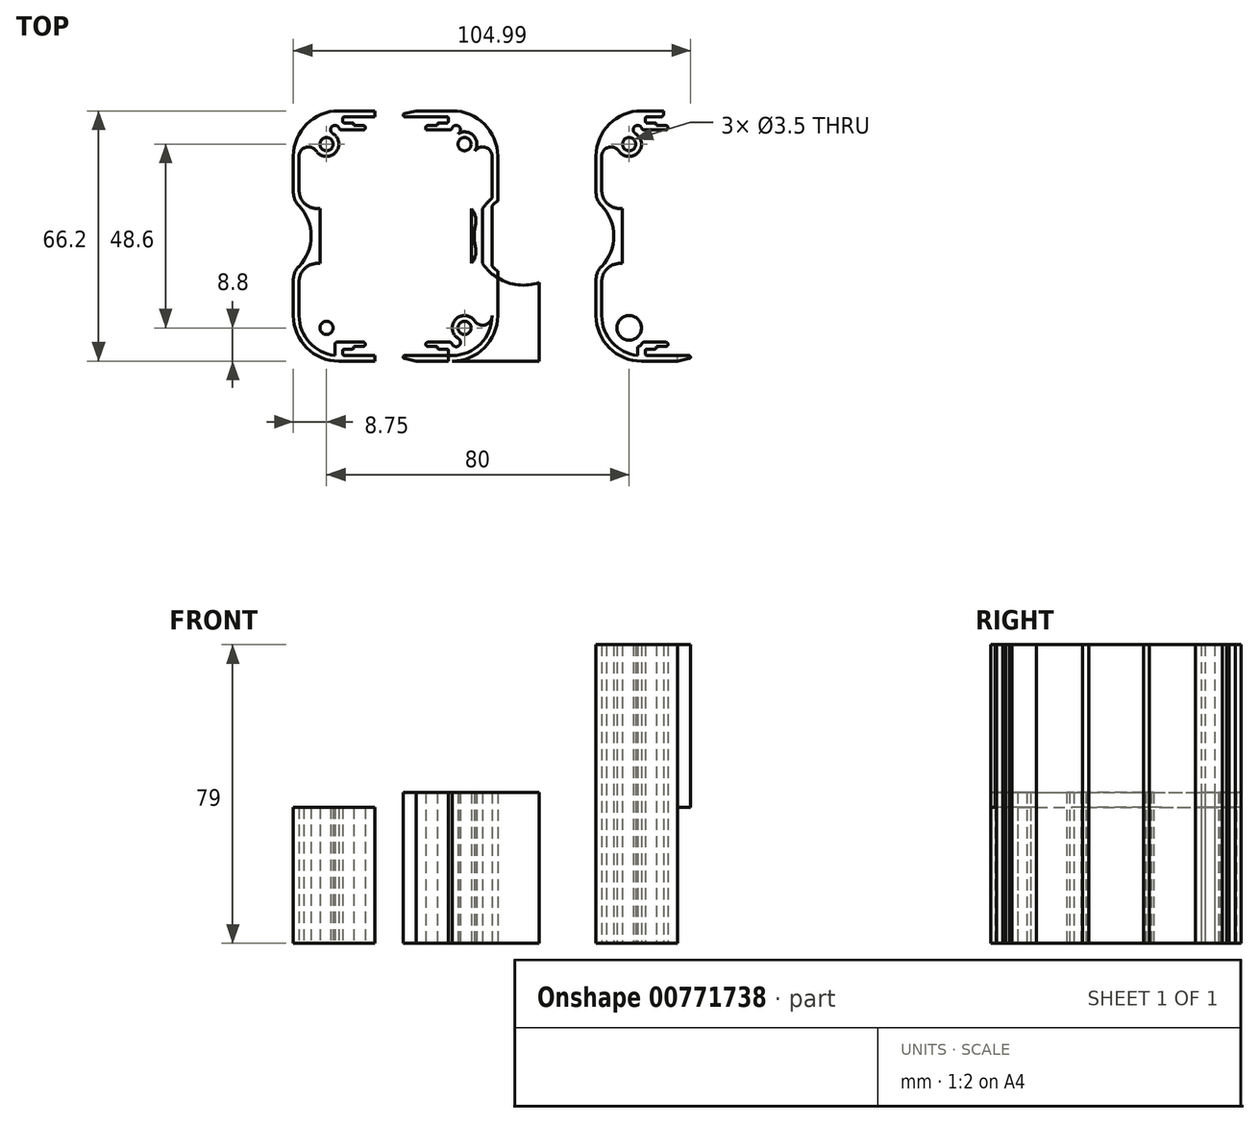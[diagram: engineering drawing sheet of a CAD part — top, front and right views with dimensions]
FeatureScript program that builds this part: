
annotation { "Feature Type Name" : "Feature", "Feature Type Description" : "" }
export const myFeature = defineFeature(function(context is Context, id is Id, definition is map)
    precondition{}
    {
        {
            var Q0;
            Q0=qCreatedBy(makeId("Top.planeOp"),FACE);
            var sketch = newSketch(context, id + "F0", { "sketchPlane" : qUnion([Q0])});
            skLineSegment(sketch, "E0.bottom", {"start": v(18, -33.1) * mm, "end": v(5, -33.1) * mm});
            skLineSegment(sketch, "E0.top", {"start": v(18, 33.1) * mm, "end": v(-18, 33.1) * mm});
            skLineSegment(sketch, "E0.left", {"start": v(18, -33.1) * mm, "end": v(18, 33.1) * mm});
            skLineSegment(sketch, "E0.right", {"start": v(-18, -33.1) * mm, "end": v(-18, 33.1) * mm});
            skPoint(sketch, "E0.middle", {"position": v(0, 0) * mm});
            skLineSegment(sketch, "E1.bottom", {"start": v(18, -33.1) * mm, "end": v(-18, -33.1) * mm});
            skLineSegment(sketch, "E1.right", {"start": v(-7, -21.1) * mm, "end": v(-7, 21.1) * mm});
            skPoint(sketch, "E2.visualSharp", {"position": v(-7, 33.1) * mm});
            skArc(sketch, "E2.filletArc", {"start": v(5, 33.1) * mm, "mid": v(-3.49, 29.59) * mm, "end": v(-7, 21.1) * mm});
            skPoint(sketch, "E3.newPointB", {"position": v(-18, -33.1) * mm});
            skArc(sketch, "E3.filletArc", {"start": v(-7, -21.1) * mm, "mid": v(-3.49, -29.59) * mm, "end": v(5, -33.1) * mm});
            skLineSegment(sketch, "E4.0", {"start": v(18, -31.6) * mm, "end": v(5, -31.6) * mm});
            skLineSegment(sketch, "E4.1", {"start": v(18, 31.55) * mm, "end": v(4, 31.55) * mm});
            skArc(sketch, "E4.2", {"start": v(4, 31.55) * mm, "mid": v(-2.77, 28.16) * mm, "end": v(-5.5, 21.1) * mm});
            skLineSegment(sketch, "E4.3", {"start": v(-5.5, -21.1) * mm, "end": v(-5.5, 21.1) * mm});
            skArc(sketch, "E4.4", {"start": v(-5.5, -21.1) * mm, "mid": v(-2.42, -28.52) * mm, "end": v(5, -31.6) * mm});
            skCircle(sketch, "E5", {"center": v(-13.8, 0) * mm, "radius": 11.5 * mm});
            skCircle(sketch, "E6.0", {"center": v(-13.8, 0) * mm, "radius": 13 * mm});
            skLineSegment(sketch, "E7", {"start": v(-2.3, 0) * mm, "end": v(-0.8, 0) * mm, "construction": true});
            skLineSegment(sketch, "E8.left", {"start": v(0, 7.25) * mm, "end": v(0, -7.25) * mm});
            skPoint(sketch, "E8.middle", {"position": v(-1.55, 0) * mm});
            skCircle(sketch, "E9", {"center": v(1.75, 24.3) * mm, "radius": 1.75 * mm});
            skCircle(sketch, "E10.0", {"center": v(1.75, 24.3) * mm, "radius": 3.25 * mm});
            skLineSegment(sketch, "E11.top", {"start": v(12, 28.1) * mm, "end": v(4, 28.1) * mm});
            skLineSegment(sketch, "E11.right", {"start": v(4, 33.1) * mm, "end": v(4, 28.1) * mm});
            skLineSegment(sketch, "E12.bottom", {"start": v(4, 28.1) * mm, "end": v(12, 28.1) * mm});
            skLineSegment(sketch, "E13.top", {"start": v(18, 31.55) * mm, "end": v(18, 31.55) * mm});
            skLineSegment(sketch, "E13.left", {"start": v(18, 31.55) * mm, "end": v(18, 31.55) * mm});
            skLineSegment(sketch, "E14.left", {"start": v(4, 28.1) * mm, "end": v(4, 31.55) * mm});
            skLineSegment(sketch, "E14.right", {"start": v(6, 29.9) * mm, "end": v(6, 33.1) * mm});
            skLineSegment(sketch, "E15.bottom", {"start": v(4, 28.1) * mm, "end": v(4, 28.1) * mm});
            skLineSegment(sketch, "E15.top", {"start": v(6, 29.9) * mm, "end": v(9, 29.9) * mm});
            skLineSegment(sketch, "E15.right", {"start": v(9, 29.2) * mm, "end": v(9, 29.9) * mm});
            skLineSegment(sketch, "E16.top", {"start": v(9, 29.2) * mm, "end": v(12, 29.2) * mm});
            skLineSegment(sketch, "E16.right", {"start": v(12, 28.1) * mm, "end": v(12, 29.2) * mm});
            skCircle(sketch, "E17", {"center": v(-3.01, 21.1) * mm, "radius": 2.49 * mm});
            skPoint(sketch, "E17.second.point", {"position": v(-5.5, 21.1) * mm});
            skPoint(sketch, "E17.third.point", {"position": v(-5.5, 21.1) * mm});
            skCircle(sketch, "E18", {"center": v(4, 28.1) * mm, "radius": 1.17 * mm});
            skLineSegment(sketch, "E19", {"start": v(4, 28.1) * mm, "end": v(4.82, 28.92) * mm, "construction": true});
            skLineSegment(sketch, "E20.bottom", {"start": v(4, 33.1) * mm, "end": v(10.8, 33.1) * mm});
            skLineSegment(sketch, "E20.top", {"start": v(4, 31.55) * mm, "end": v(10.8, 31.55) * mm});
            skLineSegment(sketch, "E20.left", {"start": v(4, 33.1) * mm, "end": v(4, 31.55) * mm});
            skLineSegment(sketch, "E20.right", {"start": v(10.8, 33.1) * mm, "end": v(10.8, 31.55) * mm});
            skLineSegment(sketch, "E21", {"start": v(14.5, 33.1) * mm, "end": v(18, 32.33) * mm});
            skLineSegment(sketch, "E22", {"start": v(18, 33.1) * mm, "end": v(18, 31.55) * mm, "construction": true});
            skLineSegment(sketch, "E23", {"start": v(18, 0) * mm, "end": v(-26.8, 0) * mm, "construction": true});
            skCircle(sketch, "E24.MirrorC", {"center": v(-3.01, -21.1) * mm, "radius": 2.49 * mm});
            skCircle(sketch, "E25.MirrorC", {"center": v(1.75, -24.3) * mm, "radius": 3.25 * mm});
            skCircle(sketch, "E26.MirrorC", {"center": v(1.75, -24.3) * mm, "radius": 1.75 * mm});
            skCircle(sketch, "E27.MirrorC", {"center": v(4, -28.1) * mm, "radius": 1.17 * mm});
            skLineSegment(sketch, "E28.MirrorCS", {"start": v(4, -28.1) * mm, "end": v(4, -31.55) * mm});
            skLineSegment(sketch, "E29.MirrorCS", {"start": v(4, -28.1) * mm, "end": v(12, -28.1) * mm});
            skLineSegment(sketch, "E30.MirrorCS", {"start": v(12, -28.1) * mm, "end": v(12, -29.2) * mm});
            skLineSegment(sketch, "E31.MirrorCS", {"start": v(9, -29.2) * mm, "end": v(12, -29.2) * mm});
            skLineSegment(sketch, "E32.MirrorCS", {"start": v(9, -29.2) * mm, "end": v(9, -29.9) * mm});
            skLineSegment(sketch, "E33.MirrorCS", {"start": v(6, -29.9) * mm, "end": v(9, -29.9) * mm});
            skLineSegment(sketch, "E34.MirrorCS", {"start": v(6, -29.9) * mm, "end": v(6, -33.1) * mm});
            skLineSegment(sketch, "E35.MirrorCS", {"start": v(14.5, -33.1) * mm, "end": v(18, -32.33) * mm});
            skLineSegment(sketch, "E36.bottom", {"start": v(18, 33.1) * mm, "end": v(-5.5, 33.1) * mm, "construction": true});
            skLineSegment(sketch, "E36.top", {"start": v(18, 21.1) * mm, "end": v(-5.5, 21.1) * mm, "construction": true});
            skLineSegment(sketch, "E36.left", {"start": v(18, 33.1) * mm, "end": v(18, 21.1) * mm, "construction": true});
            skLineSegment(sketch, "E36.right", {"start": v(-5.5, 33.1) * mm, "end": v(-5.5, 21.1) * mm, "construction": true});
            skLineSegment(sketch, "E37", {"start": v(0, 7.25) * mm, "end": v(-3, 7.25) * mm});
            skLineSegment(sketch, "E38", {"start": v(-3, 7.25) * mm, "end": v(-3, -7.25) * mm});
            skLineSegment(sketch, "E39", {"start": v(-3, -7.25) * mm, "end": v(0, -7.25) * mm});
            skLineSegment(sketch, "E40", {"start": v(-5.5, 21.1) * mm, "end": v(1.75, 24.3) * mm, "construction": true});
            skLineSegment(sketch, "E41", {"start": v(0, 0) * mm, "end": v(-130, 0) * mm, "construction": true});
            skLineSegment(sketch, "E42", {"start": v(-20, 48.28) * mm, "end": v(-20, -53.57) * mm, "construction": true});
            skLineSegment(sketch, "E43.MirrorCS", {"start": v(-44, 28.1) * mm, "end": v(-44.82, 28.92) * mm, "construction": true});
            skLineSegment(sketch, "E44.MirrorCS", {"start": v(-44, 28.1) * mm, "end": v(-44, 31.55) * mm});
            skCircle(sketch, "E45.MirrorC", {"center": v(-44, 28.1) * mm, "radius": 1.17 * mm});
            skLineSegment(sketch, "E46.MirrorCS", {"start": v(-44, 33.1) * mm, "end": v(-44, 28.1) * mm});
            skLineSegment(sketch, "E47.MirrorCS", {"start": v(-44, 33.1) * mm, "end": v(-44, 31.55) * mm});
            skLineSegment(sketch, "E48.MirrorCS", {"start": v(-58, 33.1) * mm, "end": v(-58, 31.55) * mm, "construction": true});
            skLineSegment(sketch, "E49.MirrorCS", {"start": v(-52, 28.1) * mm, "end": v(-52, 29.2) * mm});
            skLineSegment(sketch, "E50.MirrorCS", {"start": v(-44, 28.1) * mm, "end": v(-52, 28.1) * mm});
            skLineSegment(sketch, "E51.MirrorCS", {"start": v(-50.8, 33.1) * mm, "end": v(-50.8, 31.55) * mm});
            skLineSegment(sketch, "E52.MirrorCS", {"start": v(-46, -29.9) * mm, "end": v(-46, -33.1) * mm});
            skLineSegment(sketch, "E53.MirrorCS", {"start": v(-49, -29.2) * mm, "end": v(-49, -29.9) * mm});
            skLineSegment(sketch, "E54.MirrorCS", {"start": v(-44, 31.55) * mm, "end": v(-50.8, 31.55) * mm});
            skLineSegment(sketch, "E55.MirrorCS", {"start": v(-46, 29.9) * mm, "end": v(-49, 29.9) * mm});
            skLineSegment(sketch, "E56.MirrorCS", {"start": v(-49, 29.2) * mm, "end": v(-52, 29.2) * mm});
            skLineSegment(sketch, "E57.MirrorCS", {"start": v(-52, 28.1) * mm, "end": v(-44, 28.1) * mm});
            skLineSegment(sketch, "E58.MirrorCS", {"start": v(-49, 29.2) * mm, "end": v(-49, 29.9) * mm});
            skLineSegment(sketch, "E59.MirrorCS", {"start": v(-46, 29.9) * mm, "end": v(-46, 33.1) * mm});
            skCircle(sketch, "E60.MirrorC", {"center": v(-44, -28.1) * mm, "radius": 1.17 * mm});
            skLineSegment(sketch, "E61.MirrorCS", {"start": v(-44, -28.1) * mm, "end": v(-44, -31.55) * mm});
            skLineSegment(sketch, "E62.MirrorCS", {"start": v(-40, 7.25) * mm, "end": v(-37, 7.25) * mm});
            skLineSegment(sketch, "E63.MirrorCS", {"start": v(-44, 33.1) * mm, "end": v(-50.8, 33.1) * mm});
            skLineSegment(sketch, "E64.MirrorCS", {"start": v(-46, -29.9) * mm, "end": v(-49, -29.9) * mm});
            skLineSegment(sketch, "E65.MirrorCS", {"start": v(-52, -28.1) * mm, "end": v(-52, -29.2) * mm});
            skLineSegment(sketch, "E66.MirrorCS", {"start": v(-54.5, 33.1) * mm, "end": v(-58, 32.33) * mm});
            skLineSegment(sketch, "E67.MirrorCS", {"start": v(-49, -29.2) * mm, "end": v(-52, -29.2) * mm});
            skLineSegment(sketch, "E68.MirrorCS", {"start": v(-37, -7.25) * mm, "end": v(-40, -7.25) * mm});
            skLineSegment(sketch, "E69.MirrorCS", {"start": v(-58, 31.55) * mm, "end": v(-44, 31.55) * mm});
            skCircle(sketch, "E70.MirrorC", {"center": v(-41.75, 24.3) * mm, "radius": 1.75 * mm});
            skCircle(sketch, "E71.MirrorC", {"center": v(-41.75, 24.3) * mm, "radius": 3.25 * mm});
            skPoint(sketch, "E72.MirrorP", {"position": v(-34.5, 21.1) * mm});
            skLineSegment(sketch, "E73.MirrorCS", {"start": v(-37.7, 0) * mm, "end": v(-39.2, 0) * mm, "construction": true});
            skLineSegment(sketch, "E74.MirrorCS", {"start": v(-44, 28.1) * mm, "end": v(-44, 28.1) * mm});
            skLineSegment(sketch, "E75.MirrorCS", {"start": v(-58, 21.1) * mm, "end": v(-34.5, 21.1) * mm, "construction": true});
            skLineSegment(sketch, "E76.MirrorCS", {"start": v(-54.5, -33.1) * mm, "end": v(-58, -32.33) * mm});
            skLineSegment(sketch, "E77.MirrorCS", {"start": v(-34.5, 21.1) * mm, "end": v(-41.75, 24.3) * mm, "construction": true});
            skLineSegment(sketch, "E78.MirrorCS", {"start": v(-58, 31.55) * mm, "end": v(-58, 31.55) * mm});
            skLineSegment(sketch, "E79.MirrorCS", {"start": v(-58, -33.1) * mm, "end": v(-45, -33.1) * mm});
            skArc(sketch, "E80.MirrorCS", {"start": v(-45, 33.1) * mm, "mid": v(-36.51, 29.59) * mm, "end": v(-33, 21.1) * mm});
            skArc(sketch, "E81.MirrorCS", {"start": v(-33, -21.1) * mm, "mid": v(-36.51, -29.59) * mm, "end": v(-45, -33.1) * mm});
            skLineSegment(sketch, "E82.MirrorCS", {"start": v(-58, -31.6) * mm, "end": v(-45, -31.6) * mm});
            skArc(sketch, "E83.MirrorCS", {"start": v(-44, 31.55) * mm, "mid": v(-37.23, 28.16) * mm, "end": v(-34.5, 21.1) * mm});
            skLineSegment(sketch, "E84.MirrorCS", {"start": v(-34.5, -21.1) * mm, "end": v(-34.5, 21.1) * mm});
            skArc(sketch, "E85.MirrorCS", {"start": v(-34.5, -21.1) * mm, "mid": v(-37.58, -28.52) * mm, "end": v(-45, -31.6) * mm});
            skCircle(sketch, "E86.MirrorC", {"center": v(-26.2, 0) * mm, "radius": 13 * mm});
            skLineSegment(sketch, "E87.MirrorCS", {"start": v(-58, 33.1) * mm, "end": v(-34.5, 33.1) * mm, "construction": true});
            skCircle(sketch, "E88.MirrorC", {"center": v(-36.99, -21.1) * mm, "radius": 2.49 * mm});
            skCircle(sketch, "E89.MirrorC", {"center": v(-36.99, 21.1) * mm, "radius": 2.49 * mm});
            skCircle(sketch, "E90.MirrorC", {"center": v(-41.75, -24.3) * mm, "radius": 1.75 * mm});
            skLineSegment(sketch, "E91.MirrorCS", {"start": v(-58, 33.1) * mm, "end": v(-58, 21.1) * mm, "construction": true});
            skLineSegment(sketch, "E92.MirrorCS", {"start": v(-44, -28.1) * mm, "end": v(-52, -28.1) * mm});
            skLineSegment(sketch, "E93.MirrorCS", {"start": v(-37, 7.25) * mm, "end": v(-37, -7.25) * mm});
            skLineSegment(sketch, "E94.MirrorCS", {"start": v(-58, -33.1) * mm, "end": v(-58, 33.1) * mm});
            skLineSegment(sketch, "E95.MirrorCS", {"start": v(-40, 7.25) * mm, "end": v(-40, -7.25) * mm});
            skLineSegment(sketch, "E96.MirrorCS", {"start": v(-34.5, 33.1) * mm, "end": v(-34.5, 21.1) * mm, "construction": true});
            skPoint(sketch, "E97.MirrorP", {"position": v(-33, 33.1) * mm});
            skCircle(sketch, "E98.MirrorC", {"center": v(-26.2, 0) * mm, "radius": 11.5 * mm});
            skLineSegment(sketch, "E99.MirrorCS", {"start": v(-40, 0) * mm, "end": v(90, 0) * mm, "construction": true});
            skLineSegment(sketch, "E100.MirrorCS", {"start": v(-58, -33.1) * mm, "end": v(-22, -33.1) * mm});
            skPoint(sketch, "E101.MirrorP", {"position": v(-22, -33.1) * mm});
            skLineSegment(sketch, "E102.MirrorCS", {"start": v(-33, -21.1) * mm, "end": v(-33, 21.1) * mm});
            skLineSegment(sketch, "E103.MirrorCS", {"start": v(-58, 33.1) * mm, "end": v(-22, 33.1) * mm});
            skCircle(sketch, "E104.MirrorC", {"center": v(-41.75, -24.3) * mm, "radius": 3.25 * mm});
            skPoint(sketch, "E105.MirrorP", {"position": v(-38.45, 0) * mm});
            skLineSegment(sketch, "E106.MirrorCS", {"start": v(-22, -33.1) * mm, "end": v(-22, 33.1) * mm});
            skLineSegment(sketch, "E107.MirrorCS", {"start": v(-58, 0) * mm, "end": v(-13.2, 0) * mm, "construction": true});
            skPoint(sketch, "E108.MirrorP", {"position": v(-40, 0) * mm});
            skLineSegment(sketch, "E109", {"start": v(-60, 37.54) * mm, "end": v(-60, -51.76) * mm, "construction": true});
            skCircle(sketch, "E110.MirrorC", {"center": v(-76, 28.1) * mm, "radius": 1.17 * mm});
            skLineSegment(sketch, "E111.MirrorCS", {"start": v(-76, 28.1) * mm, "end": v(-76, 31.55) * mm});
            skLineSegment(sketch, "E112.MirrorCS", {"start": v(-76, 28.1) * mm, "end": v(-75.18, 28.92) * mm, "construction": true});
            skLineSegment(sketch, "E113.MirrorCS", {"start": v(-76, 33.1) * mm, "end": v(-76, 31.55) * mm});
            skLineSegment(sketch, "E114.MirrorCS", {"start": v(-76, 33.1) * mm, "end": v(-76, 28.1) * mm});
            skLineSegment(sketch, "E115.MirrorCS", {"start": v(-62, 33.1) * mm, "end": v(-62, 31.55) * mm, "construction": true});
            skLineSegment(sketch, "E116.MirrorCS", {"start": v(-68, 28.1) * mm, "end": v(-68, 29.2) * mm});
            skLineSegment(sketch, "E117.MirrorCS", {"start": v(-68, 28.1) * mm, "end": v(-76, 28.1) * mm});
            skCircle(sketch, "E118.MirrorC", {"center": v(-76, -28.1) * mm, "radius": 1.17 * mm});
            skLineSegment(sketch, "E119.MirrorCS", {"start": v(-76, -28.1) * mm, "end": v(-76, -31.55) * mm});
            skLineSegment(sketch, "E120.MirrorCS", {"start": v(-76, 28.1) * mm, "end": v(-68, 28.1) * mm});
            skLineSegment(sketch, "E121.MirrorCS", {"start": v(-71, 29.2) * mm, "end": v(-71, 29.9) * mm});
            skLineSegment(sketch, "E122.MirrorCS", {"start": v(-71, 29.2) * mm, "end": v(-68, 29.2) * mm});
            skLineSegment(sketch, "E123.MirrorCS", {"start": v(-74, 29.9) * mm, "end": v(-71, 29.9) * mm});
            skLineSegment(sketch, "E124.MirrorCS", {"start": v(-83, -7.25) * mm, "end": v(-80, -7.25) * mm});
            skLineSegment(sketch, "E125.MirrorCS", {"start": v(-69.2, 33.1) * mm, "end": v(-69.2, 31.55) * mm});
            skLineSegment(sketch, "E126.MirrorCS", {"start": v(-74, -29.9) * mm, "end": v(-74, -33.1) * mm});
            skLineSegment(sketch, "E127.MirrorCS", {"start": v(-68, -28.1) * mm, "end": v(-68, -29.2) * mm});
            skLineSegment(sketch, "E128.MirrorCS", {"start": v(-76, -28.1) * mm, "end": v(-68, -28.1) * mm});
            skLineSegment(sketch, "E129.MirrorCS", {"start": v(-80, 7.25) * mm, "end": v(-83, 7.25) * mm});
            skLineSegment(sketch, "E130.MirrorCS", {"start": v(-74, -29.9) * mm, "end": v(-71, -29.9) * mm});
            skLineSegment(sketch, "E131.MirrorCS", {"start": v(-71, -29.2) * mm, "end": v(-71, -29.9) * mm});
            skLineSegment(sketch, "E132.MirrorCS", {"start": v(-74, 29.9) * mm, "end": v(-74, 33.1) * mm});
            skLineSegment(sketch, "E133.MirrorCS", {"start": v(-71, -29.2) * mm, "end": v(-68, -29.2) * mm});
            skLineSegment(sketch, "E134.MirrorCS", {"start": v(-76, 33.1) * mm, "end": v(-69.2, 33.1) * mm});
            skLineSegment(sketch, "E135.MirrorCS", {"start": v(-82.3, 0) * mm, "end": v(-80.8, 0) * mm, "construction": true});
            skPoint(sketch, "E136.MirrorP", {"position": v(-85.5, 21.1) * mm});
            skLineSegment(sketch, "E137.MirrorCS", {"start": v(-62, 31.55) * mm, "end": v(-62, 31.55) * mm});
            skLineSegment(sketch, "E138.MirrorCS", {"start": v(-62, 31.55) * mm, "end": v(-76, 31.55) * mm});
            skLineSegment(sketch, "E139.MirrorCS", {"start": v(-65.5, -33.1) * mm, "end": v(-62, -32.33) * mm});
            skLineSegment(sketch, "E140.MirrorCS", {"start": v(-65.5, 33.1) * mm, "end": v(-62, 32.33) * mm});
            skLineSegment(sketch, "E141.MirrorCS", {"start": v(-80, 7.25) * mm, "end": v(-80, -7.25) * mm});
            skPoint(sketch, "E142.MirrorP", {"position": v(-98, -33.1) * mm});
            skPoint(sketch, "E143.MirrorP", {"position": v(-80, 0) * mm});
            skLineSegment(sketch, "E144.MirrorCS", {"start": v(-76, 31.55) * mm, "end": v(-69.2, 31.55) * mm});
            skLineSegment(sketch, "E145.MirrorCS", {"start": v(-85.5, 21.1) * mm, "end": v(-78.25, 24.3) * mm, "construction": true});
            skCircle(sketch, "E146.MirrorC", {"center": v(-78.25, 24.3) * mm, "radius": 3.25 * mm});
            skCircle(sketch, "E147.MirrorC", {"center": v(-83.01, -21.1) * mm, "radius": 2.49 * mm});
            skCircle(sketch, "E148.MirrorC", {"center": v(-93.8, 0) * mm, "radius": 11.5 * mm});
            skLineSegment(sketch, "E149.MirrorCS", {"start": v(-87, -21.1) * mm, "end": v(-87, 21.1) * mm});
            skLineSegment(sketch, "E150.MirrorCS", {"start": v(-62, 33.1) * mm, "end": v(-98, 33.1) * mm});
            skPoint(sketch, "E151.MirrorP", {"position": v(-81.55, 0) * mm});
            skLineSegment(sketch, "E152.MirrorCS", {"start": v(-62, -33.1) * mm, "end": v(-98, -33.1) * mm});
            skCircle(sketch, "E153.MirrorC", {"center": v(-83.01, 21.1) * mm, "radius": 2.49 * mm});
            skCircle(sketch, "E154.MirrorC", {"center": v(-78.25, -24.3) * mm, "radius": 1.75 * mm});
            skCircle(sketch, "E155.MirrorC", {"center": v(-93.8, 0) * mm, "radius": 13 * mm});
            skLineSegment(sketch, "E156.MirrorCS", {"start": v(-62, 33.1) * mm, "end": v(-62, 21.1) * mm, "construction": true});
            skArc(sketch, "E157.MirrorCS", {"start": v(-87, -21.1) * mm, "mid": v(-83.49, -29.59) * mm, "end": v(-75, -33.1) * mm});
            skLineSegment(sketch, "E158.MirrorCS", {"start": v(-76, 28.1) * mm, "end": v(-76, 28.1) * mm});
            skCircle(sketch, "E159.MirrorC", {"center": v(-78.25, -24.3) * mm, "radius": 3.25 * mm});
            skLineSegment(sketch, "E160.MirrorCS", {"start": v(-62, -33.1) * mm, "end": v(-75, -33.1) * mm});
            skCircle(sketch, "E161.MirrorC", {"center": v(-78.25, 24.3) * mm, "radius": 1.75 * mm});
            skArc(sketch, "E162.MirrorCS", {"start": v(-75, 33.1) * mm, "mid": v(-83.49, 29.59) * mm, "end": v(-87, 21.1) * mm});
            skLineSegment(sketch, "E163.MirrorCS", {"start": v(-98, -33.1) * mm, "end": v(-98, 33.1) * mm});
            skPoint(sketch, "E164.MirrorP", {"position": v(-87, 33.1) * mm});
            skLineSegment(sketch, "E165.MirrorCS", {"start": v(-62, 0) * mm, "end": v(-106.8, 0) * mm, "construction": true});
            skLineSegment(sketch, "E166.MirrorCS", {"start": v(-62, 21.1) * mm, "end": v(-85.5, 21.1) * mm, "construction": true});
            skLineSegment(sketch, "E167.MirrorCS", {"start": v(-62, 33.1) * mm, "end": v(-85.5, 33.1) * mm, "construction": true});
            skArc(sketch, "E168.MirrorCS", {"start": v(-76, 31.55) * mm, "mid": v(-82.77, 28.16) * mm, "end": v(-85.5, 21.1) * mm});
            skLineSegment(sketch, "E169.MirrorCS", {"start": v(-83, 7.25) * mm, "end": v(-83, -7.25) * mm});
            skLineSegment(sketch, "E170.MirrorCS", {"start": v(-62, -31.6) * mm, "end": v(-75, -31.6) * mm});
            skLineSegment(sketch, "E171.MirrorCS", {"start": v(-85.5, -21.1) * mm, "end": v(-85.5, 21.1) * mm});
            skArc(sketch, "E172.MirrorCS", {"start": v(-85.5, -21.1) * mm, "mid": v(-82.42, -28.52) * mm, "end": v(-75, -31.6) * mm});
            skLineSegment(sketch, "E173.MirrorCS", {"start": v(-62, -33.1) * mm, "end": v(-62, 33.1) * mm});
            skLineSegment(sketch, "E174.MirrorCS", {"start": v(-85.5, 33.1) * mm, "end": v(-85.5, 21.1) * mm, "construction": true});
            skSolve(sketch);
        }
        {
            var Q0;
            {var subQ0=sQuery(id+"F0.wireOp",EDGE,"E5");var subQ1=sQuery(id+"F0.wireOp",EDGE,"E1.right");var subQ2=makeQuery(id+"F0.imprint","INTERSECT",VERTEX,{"disambiguationData":[OD(1.0)],"derivedFrom":[subQ1,subQ0]});Q0=makeQuery(id+"F0.imprint","IMPRINT",FACE,{"disambiguationData":[TD([[makeQuery(id+"F0.imprint","IMPRINT",EDGE,{"disambiguationData":[TD([[subQ2,-1.0]])],"derivedFrom":subQ1}),-1.0]])]});}
            var Q1;
            {var subQ1=sQuery(id+"F0.wireOp",EDGE,"E4.2");Q1=makeQuery(id+"F0.imprint","IMPRINT",FACE,{"disambiguationData":[TD([[makeQuery(id+"F0.imprint","IMPRINT",EDGE,{"derivedFrom":subQ1}),-1.0]])]});}
            var Q2;
            {var subQ0=sQuery(id+"F0.wireOp",EDGE,"E5");var subQ1=sQuery(id+"F0.wireOp",EDGE,"E4.3");var subQ2=makeQuery(id+"F0.imprint","INTERSECT",VERTEX,{"disambiguationData":[OD(1.0)],"derivedFrom":[subQ1,subQ0]});Q2=makeQuery(id+"F0.imprint","IMPRINT",FACE,{"disambiguationData":[TD([[makeQuery(id+"F0.imprint","IMPRINT",EDGE,{"disambiguationData":[TD([[subQ2,-1.0]])],"derivedFrom":subQ1}),-1.0]])]});}
            var Q3;
            {var subQ0=sQuery(id+"F0.wireOp",EDGE,"E38");var subQ1=sQuery(id+"F0.wireOp",EDGE,"E5");var subQ2=makeQuery(id+"F0.imprint","INTERSECT",VERTEX,{"disambiguationData":[OD(0.0)],"derivedFrom":[subQ1,subQ0]});Q3=makeQuery(id+"F0.imprint","IMPRINT",FACE,{"disambiguationData":[TD([[makeQuery(id+"F0.imprint","IMPRINT",EDGE,{"disambiguationData":[TD([[subQ2,1.0]])],"derivedFrom":subQ1}),-1.0]])]});}
            var Q4;
            {var subQ0=sQuery(id+"F0.wireOp",EDGE,"E6.0");var subQ1=sQuery(id+"F0.wireOp",EDGE,"E4.3");var subQ2=makeQuery(id+"F0.imprint","INTERSECT",VERTEX,{"disambiguationData":[OD(0.0)],"derivedFrom":[subQ1,subQ0]});Q4=makeQuery(id+"F0.imprint","IMPRINT",FACE,{"disambiguationData":[TD([[makeQuery(id+"F0.imprint","IMPRINT",EDGE,{"disambiguationData":[TD([[subQ2,-1.0]])],"derivedFrom":subQ1}),-1.0]])]});}
            var Q5;
            {var subQ0=sQuery(id+"F0.wireOp",EDGE,"E6.0");var subQ1=sQuery(id+"F0.wireOp",EDGE,"E1.right");var subQ2=makeQuery(id+"F0.imprint","INTERSECT",VERTEX,{"disambiguationData":[OD(0.0)],"derivedFrom":[subQ1,subQ0]});Q5=makeQuery(id+"F0.imprint","IMPRINT",FACE,{"disambiguationData":[TD([[makeQuery(id+"F0.imprint","IMPRINT",EDGE,{"disambiguationData":[TD([[subQ2,-1.0]])],"derivedFrom":subQ1}),-1.0]])]});}
            var Q6;
            {var subQ5=sQuery(id+"F0.wireOp",EDGE,"E3.filletArc");Q6=makeQuery(id+"F0.imprint","IMPRINT",FACE,{"disambiguationData":[TD([[makeQuery(id+"F0.imprint","IMPRINT",EDGE,{"derivedFrom":subQ5}),1.0]])]});}
            var Q7;
            {var subQ1=sQuery(id+"F0.wireOp",EDGE,"E25.MirrorC");var subQ5=sQuery(id+"F0.wireOp",EDGE,"E24.MirrorC");var subQ6=makeQuery(id+"F0.imprint","INTERSECT",VERTEX,{"derivedFrom":[subQ5,subQ1]});Q7=makeQuery(id+"F0.imprint","IMPRINT",FACE,{"disambiguationData":[TD([[makeQuery(id+"F0.imprint","IMPRINT",EDGE,{"disambiguationData":[TD([[subQ6,1.0]])],"derivedFrom":subQ1}),1.0]])]});}
            var Q8;
            Q8=makeQuery(id+"F0.imprint","IMPRINT",FACE,{"disambiguationData":[TD([[makeQuery(id+"F0.imprint","IMPRINT",EDGE,{"derivedFrom":sQuery(id+"F0.wireOp",EDGE,"E26.MirrorC")}),1.0]])]});
            var Q9;
            {var subQ12=sQuery(id+"F0.wireOp",EDGE,"E30.MirrorCS");Q9=makeQuery(id+"F0.imprint","IMPRINT",FACE,{"disambiguationData":[TD([[makeQuery(id+"F0.imprint","IMPRINT",EDGE,{"derivedFrom":subQ12}),-1.0]])]});}
            var Q10;
            {var subQ7=sQuery(id+"F0.wireOp",EDGE,"E35.MirrorCS");Q10=makeQuery(id+"F0.imprint","IMPRINT",FACE,{"disambiguationData":[TD([[makeQuery(id+"F0.imprint","IMPRINT",EDGE,{"derivedFrom":subQ7}),1.0]])]});}
            var Q11;
            {var subQ1=sQuery(id+"F0.wireOp",EDGE,"E4.2");Q11=makeQuery(id+"F0.imprint","IMPRINT",FACE,{"disambiguationData":[TD([[makeQuery(id+"F0.imprint","IMPRINT",EDGE,{"derivedFrom":subQ1}),1.0]])]});}
            var Q12;
            Q12=makeQuery(id+"F0.imprint","IMPRINT",FACE,{"disambiguationData":[TD([[makeQuery(id+"F0.imprint","IMPRINT",EDGE,{"derivedFrom":sQuery(id+"F0.wireOp",EDGE,"E9")}),-1.0]])]});
            var Q13;
            {var subQ0=sQuery(id+"F0.wireOp",EDGE,"E15.top");Q13=makeQuery(id+"F0.imprint","IMPRINT",FACE,{"disambiguationData":[TD([[makeQuery(id+"F0.imprint","IMPRINT",EDGE,{"derivedFrom":subQ0}),-1.0]])]});}
            var Q14;
            {var subQ5=sQuery(id+"F0.wireOp",EDGE,"E20.right");Q14=makeQuery(id+"F0.imprint","IMPRINT",FACE,{"disambiguationData":[TD([[makeQuery(id+"F0.imprint","IMPRINT",EDGE,{"derivedFrom":subQ5}),-1.0]])]});}
            var Q15;
            {var subQ3=sQuery(id+"F0.wireOp",EDGE,"E4.1");Q15=makeQuery(id+"F0.imprint","IMPRINT",FACE,{"disambiguationData":[TD([[makeQuery(id+"F0.imprint","IMPRINT",EDGE,{"derivedFrom":subQ3}),-1.0]])]});}
            var Q16;
            {var subQ5=sQuery(id+"F0.wireOp",EDGE,"E20.bottom");var subQ6=sQuery(id+"F0.wireOp",EDGE,"E2.filletArc");var subQ7=makeQuery(id+"F0.imprint","INTERSECT",VERTEX,{"derivedFrom":[subQ6,subQ5]});Q16=makeQuery(id+"F0.imprint","IMPRINT",FACE,{"disambiguationData":[TD([[makeQuery(id+"F0.imprint","IMPRINT",EDGE,{"disambiguationData":[TD([[subQ7,-1.0]])],"derivedFrom":subQ6}),1.0]])]});}
            var Q17;
            Q17=makeQuery(id+"F0.imprint","IMPRINT",FACE,{"disambiguationData":[TD([[makeQuery(id+"F0.imprint","IMPRINT",EDGE,{"derivedFrom":sQuery(id+"F0.wireOp",EDGE,"E8.left")}),-1.0]])]});
            extrude(context, id + "F1", {"entities" : qUnion([Q0, Q1, Q2, Q3, Q4, Q5, Q6, Q7, Q8, Q9, Q10, Q11, Q12, Q13, Q14, Q15, Q16, Q17]), "depth" : 79 * mm, "offsetDistance" : 25 * mm});
        }
        {
            var Q0;
            {var subQ1=sQuery(id+"F0.wireOp",EDGE,"E83.MirrorCS");Q0=makeQuery(id+"F0.imprint","IMPRINT",FACE,{"disambiguationData":[TD([[makeQuery(id+"F0.imprint","IMPRINT",EDGE,{"derivedFrom":subQ1}),1.0]])]});}
            var Q1;
            {var subQ1=sQuery(id+"F0.wireOp",EDGE,"E76.MirrorCS");Q1=makeQuery(id+"F0.imprint","IMPRINT",FACE,{"disambiguationData":[TD([[makeQuery(id+"F0.imprint","IMPRINT",EDGE,{"derivedFrom":subQ1}),-1.0]])]});}
            var Q2;
            {var subQ11=sQuery(id+"F0.wireOp",EDGE,"E81.MirrorCS");Q2=makeQuery(id+"F0.imprint","IMPRINT",FACE,{"disambiguationData":[TD([[makeQuery(id+"F0.imprint","IMPRINT",EDGE,{"derivedFrom":subQ11}),-1.0]])]});}
            var Q3;
            Q3=makeQuery(id+"F0.imprint","IMPRINT",FACE,{"disambiguationData":[TD([[makeQuery(id+"F0.imprint","IMPRINT",EDGE,{"derivedFrom":sQuery(id+"F0.wireOp",EDGE,"E53.MirrorCS")}),1.0]])]});
            var Q4;
            {var subQ1=sQuery(id+"F0.wireOp",EDGE,"E61.MirrorCS");var subQ3=sQuery(id+"F0.wireOp",EDGE,"E60.MirrorC");var subQ4=makeQuery(id+"F0.imprint","INTERSECT",VERTEX,{"derivedFrom":[subQ3,subQ1]});Q4=makeQuery(id+"F0.imprint","IMPRINT",FACE,{"disambiguationData":[TD([[makeQuery(id+"F0.imprint","IMPRINT",EDGE,{"disambiguationData":[TD([[subQ4,-1.0]])],"derivedFrom":subQ3}),-1.0]])]});}
            var Q5;
            Q5=makeQuery(id+"F0.imprint","IMPRINT",FACE,{"disambiguationData":[TD([[makeQuery(id+"F0.imprint","IMPRINT",EDGE,{"derivedFrom":sQuery(id+"F0.wireOp",EDGE,"E90.MirrorC")}),-1.0]])]});
            var Q6;
            {var subQ0=sQuery(id+"F0.wireOp",EDGE,"E86.MirrorC");var subQ1=sQuery(id+"F0.wireOp",EDGE,"E84.MirrorCS");var subQ2=makeQuery(id+"F0.imprint","INTERSECT",VERTEX,{"disambiguationData":[OD(0.0)],"derivedFrom":[subQ1,subQ0]});Q6=makeQuery(id+"F0.imprint","IMPRINT",FACE,{"disambiguationData":[TD([[makeQuery(id+"F0.imprint","IMPRINT",EDGE,{"disambiguationData":[TD([[subQ2,-1.0]])],"derivedFrom":subQ1}),-1.0]])]});}
            var Q7;
            {var subQ0=sQuery(id+"F0.wireOp",EDGE,"E86.MirrorC");var subQ1=sQuery(id+"F0.wireOp",EDGE,"E84.MirrorCS");var subQ2=makeQuery(id+"F0.imprint","INTERSECT",VERTEX,{"disambiguationData":[OD(0.0)],"derivedFrom":[subQ1,subQ0]});Q7=makeQuery(id+"F0.imprint","IMPRINT",FACE,{"disambiguationData":[TD([[makeQuery(id+"F0.imprint","IMPRINT",EDGE,{"disambiguationData":[TD([[subQ2,-1.0]])],"derivedFrom":subQ1}),1.0]])]});}
            var Q8;
            {var subQ0=sQuery(id+"F0.wireOp",EDGE,"E62.MirrorCS");Q8=makeQuery(id+"F0.imprint","IMPRINT",FACE,{"disambiguationData":[TD([[makeQuery(id+"F0.imprint","IMPRINT",EDGE,{"derivedFrom":subQ0}),-1.0]])]});}
            var Q9;
            {var subQ0=sQuery(id+"F0.wireOp",EDGE,"E93.MirrorCS");var subQ4=sQuery(id+"F0.wireOp",EDGE,"E98.MirrorC");var subQ6=makeQuery(id+"F0.imprint","INTERSECT",VERTEX,{"disambiguationData":[OD(0.0)],"derivedFrom":[subQ0,subQ4]});Q9=makeQuery(id+"F0.imprint","IMPRINT",FACE,{"disambiguationData":[TD([[makeQuery(id+"F0.imprint","IMPRINT",EDGE,{"disambiguationData":[TD([[subQ6,1.0]])],"derivedFrom":subQ4}),1.0]])]});}
            var Q10;
            {var subQ0=sQuery(id+"F0.wireOp",EDGE,"E98.MirrorC");var subQ1=sQuery(id+"F0.wireOp",EDGE,"E84.MirrorCS");var subQ2=makeQuery(id+"F0.imprint","INTERSECT",VERTEX,{"disambiguationData":[OD(1.0)],"derivedFrom":[subQ1,subQ0]});Q10=makeQuery(id+"F0.imprint","IMPRINT",FACE,{"disambiguationData":[TD([[makeQuery(id+"F0.imprint","IMPRINT",EDGE,{"disambiguationData":[TD([[subQ2,-1.0]])],"derivedFrom":subQ1}),1.0]])]});}
            var Q11;
            {var subQ0=sQuery(id+"F0.wireOp",EDGE,"E98.MirrorC");var subQ1=sQuery(id+"F0.wireOp",EDGE,"E84.MirrorCS");var subQ2=makeQuery(id+"F0.imprint","INTERSECT",VERTEX,{"disambiguationData":[OD(1.0)],"derivedFrom":[subQ1,subQ0]});Q11=makeQuery(id+"F0.imprint","IMPRINT",FACE,{"disambiguationData":[TD([[makeQuery(id+"F0.imprint","IMPRINT",EDGE,{"disambiguationData":[TD([[subQ2,-1.0]])],"derivedFrom":subQ1}),-1.0]])]});}
            var Q12;
            {var subQ0=sQuery(id+"F0.wireOp",EDGE,"E83.MirrorCS");Q12=makeQuery(id+"F0.imprint","IMPRINT",FACE,{"disambiguationData":[TD([[makeQuery(id+"F0.imprint","IMPRINT",EDGE,{"derivedFrom":subQ0}),-1.0]])]});}
            var Q13;
            Q13=makeQuery(id+"F0.imprint","IMPRINT",FACE,{"disambiguationData":[TD([[makeQuery(id+"F0.imprint","IMPRINT",EDGE,{"derivedFrom":sQuery(id+"F0.wireOp",EDGE,"E70.MirrorC")}),1.0]])]});
            var Q14;
            {var subQ2=sQuery(id+"F0.wireOp",EDGE,"E49.MirrorCS");Q14=makeQuery(id+"F0.imprint","IMPRINT",FACE,{"disambiguationData":[TD([[makeQuery(id+"F0.imprint","IMPRINT",EDGE,{"derivedFrom":subQ2}),-1.0]])]});}
            var Q15;
            {var subQ0=sQuery(id+"F0.wireOp",EDGE,"E51.MirrorCS");Q15=makeQuery(id+"F0.imprint","IMPRINT",FACE,{"disambiguationData":[TD([[makeQuery(id+"F0.imprint","IMPRINT",EDGE,{"derivedFrom":subQ0}),1.0]])]});}
            var Q16;
            {var subQ4=sQuery(id+"F0.wireOp",EDGE,"E51.MirrorCS");Q16=makeQuery(id+"F0.imprint","IMPRINT",FACE,{"disambiguationData":[TD([[makeQuery(id+"F0.imprint","IMPRINT",EDGE,{"derivedFrom":subQ4}),-1.0]])]});}
            var Q17;
            {var subQ0=sQuery(id+"F0.wireOp",EDGE,"E103.MirrorCS");var subQ7=sQuery(id+"F0.wireOp",EDGE,"E59.MirrorCS");var subQ9=makeQuery(id+"F0.imprint","INTERSECT",VERTEX,{"derivedFrom":[subQ7,subQ0]});Q17=makeQuery(id+"F0.imprint","IMPRINT",FACE,{"disambiguationData":[TD([[makeQuery(id+"F0.imprint","IMPRINT",EDGE,{"disambiguationData":[TD([[subQ9,1.0]])],"derivedFrom":subQ7}),-1.0]])]});}
            extrude(context, id + "F2", {"entities" : qUnion([Q0, Q1, Q2, Q3, Q4, Q5, Q6, Q7, Q8, Q9, Q10, Q11, Q12, Q13, Q14, Q15, Q16, Q17]), "depth" : 40 * mm, "offsetDistance" : 25 * mm});
        }
        {
            var Q0;
            {var subQ0=sQuery(id+"F0.wireOp",EDGE,"E157.MirrorCS");Q0=makeQuery(id+"F0.imprint","IMPRINT",FACE,{"disambiguationData":[TD([[makeQuery(id+"F0.imprint","IMPRINT",EDGE,{"derivedFrom":subQ0}),1.0]])]});}
            var Q1;
            {var subQ1=sQuery(id+"F0.wireOp",EDGE,"E125.MirrorCS");Q1=makeQuery(id+"F0.imprint","IMPRINT",FACE,{"disambiguationData":[TD([[makeQuery(id+"F0.imprint","IMPRINT",EDGE,{"derivedFrom":subQ1}),1.0]])]});}
            var Q2;
            {var subQ0=sQuery(id+"F0.wireOp",EDGE,"E125.MirrorCS");Q2=makeQuery(id+"F0.imprint","IMPRINT",FACE,{"disambiguationData":[TD([[makeQuery(id+"F0.imprint","IMPRINT",EDGE,{"derivedFrom":subQ0}),-1.0]])]});}
            var Q3;
            {var subQ3=sQuery(id+"F0.wireOp",EDGE,"E132.MirrorCS");var subQ5=sQuery(id+"F0.wireOp",EDGE,"E150.MirrorCS");var subQ6=makeQuery(id+"F0.imprint","INTERSECT",VERTEX,{"derivedFrom":[subQ3,subQ5]});Q3=makeQuery(id+"F0.imprint","IMPRINT",FACE,{"disambiguationData":[TD([[makeQuery(id+"F0.imprint","IMPRINT",EDGE,{"disambiguationData":[TD([[subQ6,1.0]])],"derivedFrom":subQ3}),1.0]])]});}
            var Q4;
            {var subQ5=sQuery(id+"F0.wireOp",EDGE,"E116.MirrorCS");Q4=makeQuery(id+"F0.imprint","IMPRINT",FACE,{"disambiguationData":[TD([[makeQuery(id+"F0.imprint","IMPRINT",EDGE,{"derivedFrom":subQ5}),1.0]])]});}
            var Q5;
            {var subQ5=sQuery(id+"F0.wireOp",EDGE,"E168.MirrorCS");Q5=makeQuery(id+"F0.imprint","IMPRINT",FACE,{"disambiguationData":[TD([[makeQuery(id+"F0.imprint","IMPRINT",EDGE,{"derivedFrom":subQ5}),1.0]])]});}
            var Q6;
            Q6=makeQuery(id+"F0.imprint","IMPRINT",FACE,{"disambiguationData":[TD([[makeQuery(id+"F0.imprint","IMPRINT",EDGE,{"derivedFrom":sQuery(id+"F0.wireOp",EDGE,"E161.MirrorC")}),-1.0]])]});
            var Q7;
            {var subQ9=sQuery(id+"F0.wireOp",EDGE,"E168.MirrorCS");Q7=makeQuery(id+"F0.imprint","IMPRINT",FACE,{"disambiguationData":[TD([[makeQuery(id+"F0.imprint","IMPRINT",EDGE,{"derivedFrom":subQ9}),-1.0]])]});}
            var Q8;
            {var subQ0=sQuery(id+"F0.wireOp",EDGE,"E171.MirrorCS");var subQ1=sQuery(id+"F0.wireOp",EDGE,"E148.MirrorC");var subQ2=makeQuery(id+"F0.imprint","INTERSECT",VERTEX,{"disambiguationData":[OD(0.0)],"derivedFrom":[subQ1,subQ0]});Q8=makeQuery(id+"F0.imprint","IMPRINT",FACE,{"disambiguationData":[TD([[makeQuery(id+"F0.imprint","IMPRINT",EDGE,{"disambiguationData":[TD([[subQ2,-1.0]])],"derivedFrom":subQ1}),-1.0]])]});}
            var Q9;
            {var subQ0=sQuery(id+"F0.wireOp",EDGE,"E171.MirrorCS");var subQ1=sQuery(id+"F0.wireOp",EDGE,"E148.MirrorC");var subQ2=makeQuery(id+"F0.imprint","INTERSECT",VERTEX,{"disambiguationData":[OD(0.0)],"derivedFrom":[subQ1,subQ0]});Q9=makeQuery(id+"F0.imprint","IMPRINT",FACE,{"disambiguationData":[TD([[makeQuery(id+"F0.imprint","IMPRINT",EDGE,{"disambiguationData":[TD([[subQ2,1.0]])],"derivedFrom":subQ1}),-1.0]])]});}
            var Q10;
            {var subQ0=sQuery(id+"F0.wireOp",EDGE,"E169.MirrorCS");var subQ1=sQuery(id+"F0.wireOp",EDGE,"E148.MirrorC");var subQ2=makeQuery(id+"F0.imprint","INTERSECT",VERTEX,{"disambiguationData":[OD(0.0)],"derivedFrom":[subQ1,subQ0]});Q10=makeQuery(id+"F0.imprint","IMPRINT",FACE,{"disambiguationData":[TD([[makeQuery(id+"F0.imprint","IMPRINT",EDGE,{"disambiguationData":[TD([[subQ2,1.0]])],"derivedFrom":subQ1}),-1.0]])]});}
            var Q11;
            {var subQ0=sQuery(id+"F0.wireOp",EDGE,"E124.MirrorCS");Q11=makeQuery(id+"F0.imprint","IMPRINT",FACE,{"disambiguationData":[TD([[makeQuery(id+"F0.imprint","IMPRINT",EDGE,{"derivedFrom":subQ0}),1.0]])]});}
            var Q12;
            {var subQ0=sQuery(id+"F0.wireOp",EDGE,"E171.MirrorCS");var subQ1=sQuery(id+"F0.wireOp",EDGE,"E148.MirrorC");var subQ2=makeQuery(id+"F0.imprint","INTERSECT",VERTEX,{"disambiguationData":[OD(1.0)],"derivedFrom":[subQ1,subQ0]});Q12=makeQuery(id+"F0.imprint","IMPRINT",FACE,{"disambiguationData":[TD([[makeQuery(id+"F0.imprint","IMPRINT",EDGE,{"disambiguationData":[TD([[subQ2,-1.0]])],"derivedFrom":subQ1}),-1.0]])]});}
            var Q13;
            {var subQ0=sQuery(id+"F0.wireOp",EDGE,"E149.MirrorCS");var subQ1=sQuery(id+"F0.wireOp",EDGE,"E148.MirrorC");var subQ2=makeQuery(id+"F0.imprint","INTERSECT",VERTEX,{"disambiguationData":[OD(1.0)],"derivedFrom":[subQ1,subQ0]});Q13=makeQuery(id+"F0.imprint","IMPRINT",FACE,{"disambiguationData":[TD([[makeQuery(id+"F0.imprint","IMPRINT",EDGE,{"disambiguationData":[TD([[subQ2,-1.0]])],"derivedFrom":subQ1}),-1.0]])]});}
            var Q14;
            {var subQ1=sQuery(id+"F0.wireOp",EDGE,"E118.MirrorC");var subQ6=sQuery(id+"F0.wireOp",EDGE,"E119.MirrorCS");var subQ8=makeQuery(id+"F0.imprint","INTERSECT",VERTEX,{"derivedFrom":[subQ1,subQ6]});Q14=makeQuery(id+"F0.imprint","IMPRINT",FACE,{"disambiguationData":[TD([[makeQuery(id+"F0.imprint","IMPRINT",EDGE,{"disambiguationData":[TD([[subQ8,-1.0]])],"derivedFrom":subQ1}),1.0]])]});}
            var Q15;
            Q15=makeQuery(id+"F0.imprint","IMPRINT",FACE,{"disambiguationData":[TD([[makeQuery(id+"F0.imprint","IMPRINT",EDGE,{"derivedFrom":sQuery(id+"F0.wireOp",EDGE,"E154.MirrorC")}),1.0]])]});
            var Q16;
            {var subQ0=sQuery(id+"F0.wireOp",EDGE,"E127.MirrorCS");Q16=makeQuery(id+"F0.imprint","IMPRINT",FACE,{"disambiguationData":[TD([[makeQuery(id+"F0.imprint","IMPRINT",EDGE,{"derivedFrom":subQ0}),-1.0]])]});}
            var Q17;
            {var subQ7=sQuery(id+"F0.wireOp",EDGE,"E139.MirrorCS");Q17=makeQuery(id+"F0.imprint","IMPRINT",FACE,{"disambiguationData":[TD([[makeQuery(id+"F0.imprint","IMPRINT",EDGE,{"derivedFrom":subQ7}),1.0]])]});}
            extrude(context, id + "F3", {"entities" : qUnion([Q0, Q1, Q2, Q3, Q4, Q5, Q6, Q7, Q8, Q9, Q10, Q11, Q12, Q13, Q14, Q15, Q16, Q17]), "depth" : 36 * mm, "offsetDistance" : 25 * mm});
        }
        {
            var Q0;
            {var subQ0=sQuery(id+"F0.wireOp",EDGE,"E149.MirrorCS");var subQ1=sQuery(id+"F0.wireOp",EDGE,"E148.MirrorC");Q0=makeQuery(id+"F3.opExtrude","SWEPT_EDGE",EDGE,{"disambiguationData":[OSD([subQ1,subQ0]),TDD([makeQuery(id+"F0.imprint","INTERSECT",VERTEX,{"disambiguationData":[OD(0.0)],"derivedFrom":[subQ1,subQ0]})])]});}
            var Q1;
            {var subQ0=sQuery(id+"F0.wireOp",EDGE,"E149.MirrorCS");var subQ1=sQuery(id+"F0.wireOp",EDGE,"E148.MirrorC");Q1=makeQuery(id+"F3.opExtrude","SWEPT_EDGE",EDGE,{"disambiguationData":[OSD([subQ1,subQ0]),TDD([makeQuery(id+"F0.imprint","INTERSECT",VERTEX,{"disambiguationData":[OD(1.0)],"derivedFrom":[subQ1,subQ0]})])]});}
            var Q2;
            {var subQ0=sQuery(id+"F0.wireOp",EDGE,"E102.MirrorCS");var subQ1=sQuery(id+"F0.wireOp",EDGE,"E98.MirrorC");Q2=makeQuery(id+"F2.opExtrude","SWEPT_EDGE",EDGE,{"disambiguationData":[OSD([subQ1,subQ0]),TDD([makeQuery(id+"F0.imprint","INTERSECT",VERTEX,{"disambiguationData":[OD(0.0)],"derivedFrom":[subQ1,subQ0]})])]});}
            var Q3;
            {var subQ0=sQuery(id+"F0.wireOp",EDGE,"E102.MirrorCS");var subQ1=sQuery(id+"F0.wireOp",EDGE,"E98.MirrorC");Q3=makeQuery(id+"F2.opExtrude","SWEPT_EDGE",EDGE,{"disambiguationData":[OSD([subQ1,subQ0]),TDD([makeQuery(id+"F0.imprint","INTERSECT",VERTEX,{"disambiguationData":[OD(1.0)],"derivedFrom":[subQ1,subQ0]})])]});}
            var Q4;
            {var subQ0=sQuery(id+"F0.wireOp",EDGE,"E5");var subQ1=sQuery(id+"F0.wireOp",EDGE,"E1.right");Q4=makeQuery(id+"F1.opExtrude","SWEPT_EDGE",EDGE,{"disambiguationData":[OSD([subQ1,subQ0]),TDD([makeQuery(id+"F0.imprint","INTERSECT",VERTEX,{"disambiguationData":[OD(1.0)],"derivedFrom":[subQ1,subQ0]})])]});}
            var Q5;
            {var subQ0=sQuery(id+"F0.wireOp",EDGE,"E5");var subQ1=sQuery(id+"F0.wireOp",EDGE,"E1.right");Q5=makeQuery(id+"F1.opExtrude","SWEPT_EDGE",EDGE,{"disambiguationData":[OSD([subQ1,subQ0]),TDD([makeQuery(id+"F0.imprint","INTERSECT",VERTEX,{"disambiguationData":[OD(0.0)],"derivedFrom":[subQ1,subQ0]})])]});}
            var Q6;
            {var subQ0=sQuery(id+"F0.wireOp",EDGE,"E86.MirrorC");var subQ1=sQuery(id+"F0.wireOp",EDGE,"E84.MirrorCS");Q6=makeQuery(id+"F2.opExtrude","SWEPT_EDGE",EDGE,{"disambiguationData":[OSD([subQ1,subQ0]),TDD([makeQuery(id+"F0.imprint","INTERSECT",VERTEX,{"disambiguationData":[OD(1.0)],"derivedFrom":[subQ1,subQ0]})])]});}
            var Q7;
            {var subQ0=sQuery(id+"F0.wireOp",EDGE,"E86.MirrorC");var subQ1=sQuery(id+"F0.wireOp",EDGE,"E84.MirrorCS");Q7=makeQuery(id+"F2.opExtrude","SWEPT_EDGE",EDGE,{"disambiguationData":[OSD([subQ1,subQ0]),TDD([makeQuery(id+"F0.imprint","INTERSECT",VERTEX,{"disambiguationData":[OD(0.0)],"derivedFrom":[subQ1,subQ0]})])]});}
            var Q8;
            Q8=makeQuery(id+"F2.opExtrude","SWEPT_EDGE",EDGE,{"disambiguationData":[OSD([sQuery(id+"F0.wireOp",EDGE,"E68.MirrorCS"),sQuery(id+"F0.wireOp",EDGE,"E86.MirrorC"),sQuery(id+"F0.wireOp",EDGE,"E93.MirrorCS")])]});
            var Q9;
            Q9=makeQuery(id+"F2.opExtrude","SWEPT_EDGE",EDGE,{"disambiguationData":[OSD([sQuery(id+"F0.wireOp",EDGE,"E62.MirrorCS"),sQuery(id+"F0.wireOp",EDGE,"E86.MirrorC"),sQuery(id+"F0.wireOp",EDGE,"E93.MirrorCS")])]});
            var Q10;
            Q10=makeQuery(id+"F3.opExtrude","SWEPT_EDGE",EDGE,{"disambiguationData":[OSD([sQuery(id+"F0.wireOp",EDGE,"E124.MirrorCS"),sQuery(id+"F0.wireOp",EDGE,"E155.MirrorC"),sQuery(id+"F0.wireOp",EDGE,"E169.MirrorCS")])]});
            var Q11;
            {var subQ0=sQuery(id+"F0.wireOp",EDGE,"E171.MirrorCS");var subQ1=sQuery(id+"F0.wireOp",EDGE,"E155.MirrorC");Q11=makeQuery(id+"F3.opExtrude","SWEPT_EDGE",EDGE,{"disambiguationData":[OSD([subQ1,subQ0]),TDD([makeQuery(id+"F0.imprint","INTERSECT",VERTEX,{"disambiguationData":[OD(1.0)],"derivedFrom":[subQ1,subQ0]})])]});}
            var Q12;
            {var subQ0=sQuery(id+"F0.wireOp",EDGE,"E171.MirrorCS");var subQ1=sQuery(id+"F0.wireOp",EDGE,"E155.MirrorC");Q12=makeQuery(id+"F3.opExtrude","SWEPT_EDGE",EDGE,{"disambiguationData":[OSD([subQ1,subQ0]),TDD([makeQuery(id+"F0.imprint","INTERSECT",VERTEX,{"disambiguationData":[OD(0.0)],"derivedFrom":[subQ1,subQ0]})])]});}
            var Q13;
            Q13=makeQuery(id+"F3.opExtrude","SWEPT_EDGE",EDGE,{"disambiguationData":[OSD([sQuery(id+"F0.wireOp",EDGE,"E129.MirrorCS"),sQuery(id+"F0.wireOp",EDGE,"E155.MirrorC"),sQuery(id+"F0.wireOp",EDGE,"E169.MirrorCS")])]});
            var Q14;
            {var subQ0=sQuery(id+"F0.wireOp",EDGE,"E6.0");var subQ1=sQuery(id+"F0.wireOp",EDGE,"E4.3");Q14=makeQuery(id+"F1.opExtrude","SWEPT_EDGE",EDGE,{"disambiguationData":[OSD([subQ1,subQ0]),TDD([makeQuery(id+"F0.imprint","INTERSECT",VERTEX,{"disambiguationData":[OD(0.0)],"derivedFrom":[subQ1,subQ0]})])]});}
            var Q15;
            Q15=makeQuery(id+"F1.opExtrude","SWEPT_EDGE",EDGE,{"disambiguationData":[OSD([sQuery(id+"F0.wireOp",EDGE,"E6.0"),sQuery(id+"F0.wireOp",EDGE,"E38"),sQuery(id+"F0.wireOp",EDGE,"E39")])]});
            var Q16;
            {var subQ0=sQuery(id+"F0.wireOp",EDGE,"E6.0");var subQ1=sQuery(id+"F0.wireOp",EDGE,"E4.3");Q16=makeQuery(id+"F1.opExtrude","SWEPT_EDGE",EDGE,{"disambiguationData":[OSD([subQ1,subQ0]),TDD([makeQuery(id+"F0.imprint","INTERSECT",VERTEX,{"disambiguationData":[OD(1.0)],"derivedFrom":[subQ1,subQ0]})])]});}
            var Q17;
            Q17=makeQuery(id+"F1.opExtrude","SWEPT_EDGE",EDGE,{"disambiguationData":[OSD([sQuery(id+"F0.wireOp",EDGE,"E6.0"),sQuery(id+"F0.wireOp",EDGE,"E37"),sQuery(id+"F0.wireOp",EDGE,"E38")])]});
            fillet(context, id + "F4", {"entities" : qUnion([Q0, Q1, Q2, Q3, Q4, Q5, Q6, Q7, Q8, Q9, Q10, Q11, Q12, Q13, Q14, Q15, Q16, Q17]), "radius" : 5 * mm, "tangentPropagation" : true, "allowEdgeOverflow" : false});
        }
        {
            var Q0;
            Q0=makeQuery(id+"F3.opExtrude","SWEPT_EDGE",EDGE,{"disambiguationData":[OSD([sQuery(id+"F0.wireOp",EDGE,"E139.MirrorCS"),sQuery(id+"F0.wireOp",EDGE,"E173.MirrorCS")])]});
            var Q1;
            Q1=makeQuery(id+"F3.opExtrude","SWEPT_EDGE",EDGE,{"disambiguationData":[OSD([sQuery(id+"F0.wireOp",EDGE,"E170.MirrorCS"),sQuery(id+"F0.wireOp",EDGE,"E173.MirrorCS")])]});
            var Q2;
            Q2=makeQuery(id+"F3.opExtrude","SWEPT_EDGE",EDGE,{"disambiguationData":[OSD([sQuery(id+"F0.wireOp",EDGE,"E126.MirrorCS"),sQuery(id+"F0.wireOp",EDGE,"E170.MirrorCS")])]});
            var Q3;
            Q3=makeQuery(id+"F3.opExtrude","SWEPT_EDGE",EDGE,{"disambiguationData":[OSD([sQuery(id+"F0.wireOp",EDGE,"E126.MirrorCS"),sQuery(id+"F0.wireOp",EDGE,"E130.MirrorCS")])]});
            var Q4;
            Q4=makeQuery(id+"F3.opExtrude","SWEPT_EDGE",EDGE,{"disambiguationData":[OSD([sQuery(id+"F0.wireOp",EDGE,"E130.MirrorCS"),sQuery(id+"F0.wireOp",EDGE,"E131.MirrorCS")])]});
            var Q5;
            Q5=makeQuery(id+"F3.opExtrude","SWEPT_EDGE",EDGE,{"disambiguationData":[OSD([sQuery(id+"F0.wireOp",EDGE,"E127.MirrorCS"),sQuery(id+"F0.wireOp",EDGE,"E133.MirrorCS")])]});
            var Q6;
            Q6=makeQuery(id+"F3.opExtrude","SWEPT_EDGE",EDGE,{"disambiguationData":[OSD([sQuery(id+"F0.wireOp",EDGE,"E127.MirrorCS"),sQuery(id+"F0.wireOp",EDGE,"E128.MirrorCS")])]});
            var Q7;
            Q7=makeQuery(id+"F3.opExtrude","SWEPT_EDGE",EDGE,{"disambiguationData":[OSD([sQuery(id+"F0.wireOp",EDGE,"E116.MirrorCS"),sQuery(id+"F0.wireOp",EDGE,"E120.MirrorCS")])]});
            var Q8;
            Q8=makeQuery(id+"F3.opExtrude","SWEPT_EDGE",EDGE,{"disambiguationData":[OSD([sQuery(id+"F0.wireOp",EDGE,"E116.MirrorCS"),sQuery(id+"F0.wireOp",EDGE,"E122.MirrorCS")])]});
            var Q9;
            Q9=makeQuery(id+"F3.opExtrude","SWEPT_EDGE",EDGE,{"disambiguationData":[OSD([sQuery(id+"F0.wireOp",EDGE,"E110.MirrorC"),sQuery(id+"F0.wireOp",EDGE,"E120.MirrorCS")])]});
            var Q10;
            Q10=makeQuery(id+"F3.opExtrude","SWEPT_EDGE",EDGE,{"disambiguationData":[OSD([sQuery(id+"F0.wireOp",EDGE,"E118.MirrorC"),sQuery(id+"F0.wireOp",EDGE,"E128.MirrorCS")])]});
            var Q11;
            Q11=makeQuery(id+"F3.opExtrude","SWEPT_EDGE",EDGE,{"disambiguationData":[OSD([sQuery(id+"F0.wireOp",EDGE,"E140.MirrorCS"),sQuery(id+"F0.wireOp",EDGE,"E173.MirrorCS")])]});
            var Q12;
            Q12=makeQuery(id+"F3.opExtrude","SWEPT_EDGE",EDGE,{"disambiguationData":[OSD([sQuery(id+"F0.wireOp",EDGE,"E138.MirrorCS"),sQuery(id+"F0.wireOp",EDGE,"E173.MirrorCS")])]});
            var Q13;
            Q13=makeQuery(id+"F3.opExtrude","SWEPT_EDGE",EDGE,{"disambiguationData":[OSD([sQuery(id+"F0.wireOp",EDGE,"E132.MirrorCS"),sQuery(id+"F0.wireOp",EDGE,"E144.MirrorCS")])]});
            var Q14;
            Q14=makeQuery(id+"F3.opExtrude","SWEPT_EDGE",EDGE,{"disambiguationData":[OSD([sQuery(id+"F0.wireOp",EDGE,"E121.MirrorCS"),sQuery(id+"F0.wireOp",EDGE,"E123.MirrorCS")])]});
            var Q15;
            Q15=makeQuery(id+"F3.opExtrude","SWEPT_EDGE",EDGE,{"disambiguationData":[OSD([sQuery(id+"F0.wireOp",EDGE,"E123.MirrorCS"),sQuery(id+"F0.wireOp",EDGE,"E132.MirrorCS")])]});
            var Q16;
            Q16=makeQuery(id+"F2.opExtrude","SWEPT_EDGE",EDGE,{"disambiguationData":[OSD([sQuery(id+"F0.wireOp",EDGE,"E66.MirrorCS"),sQuery(id+"F0.wireOp",EDGE,"E94.MirrorCS")])]});
            var Q17;
            Q17=makeQuery(id+"F2.opExtrude","SWEPT_EDGE",EDGE,{"disambiguationData":[OSD([sQuery(id+"F0.wireOp",EDGE,"E59.MirrorCS"),sQuery(id+"F0.wireOp",EDGE,"E69.MirrorCS")])]});
            var Q18;
            Q18=makeQuery(id+"F2.opExtrude","SWEPT_EDGE",EDGE,{"disambiguationData":[OSD([sQuery(id+"F0.wireOp",EDGE,"E55.MirrorCS"),sQuery(id+"F0.wireOp",EDGE,"E59.MirrorCS")])]});
            var Q19;
            Q19=makeQuery(id+"F2.opExtrude","SWEPT_EDGE",EDGE,{"disambiguationData":[OSD([sQuery(id+"F0.wireOp",EDGE,"E55.MirrorCS"),sQuery(id+"F0.wireOp",EDGE,"E58.MirrorCS")])]});
            var Q20;
            Q20=makeQuery(id+"F2.opExtrude","SWEPT_EDGE",EDGE,{"disambiguationData":[OSD([sQuery(id+"F0.wireOp",EDGE,"E49.MirrorCS"),sQuery(id+"F0.wireOp",EDGE,"E56.MirrorCS")])]});
            var Q21;
            Q21=makeQuery(id+"F2.opExtrude","SWEPT_EDGE",EDGE,{"disambiguationData":[OSD([sQuery(id+"F0.wireOp",EDGE,"E45.MirrorC"),sQuery(id+"F0.wireOp",EDGE,"E50.MirrorCS")])]});
            var Q22;
            Q22=makeQuery(id+"F2.opExtrude","SWEPT_EDGE",EDGE,{"disambiguationData":[OSD([sQuery(id+"F0.wireOp",EDGE,"E60.MirrorC"),sQuery(id+"F0.wireOp",EDGE,"E92.MirrorCS")])]});
            var Q23;
            Q23=makeQuery(id+"F2.opExtrude","SWEPT_EDGE",EDGE,{"disambiguationData":[OSD([sQuery(id+"F0.wireOp",EDGE,"E65.MirrorCS"),sQuery(id+"F0.wireOp",EDGE,"E92.MirrorCS")])]});
            var Q24;
            Q24=makeQuery(id+"F2.opExtrude","SWEPT_EDGE",EDGE,{"disambiguationData":[OSD([sQuery(id+"F0.wireOp",EDGE,"E65.MirrorCS"),sQuery(id+"F0.wireOp",EDGE,"E67.MirrorCS")])]});
            var Q25;
            Q25=makeQuery(id+"F2.opExtrude","SWEPT_EDGE",EDGE,{"disambiguationData":[OSD([sQuery(id+"F0.wireOp",EDGE,"E53.MirrorCS"),sQuery(id+"F0.wireOp",EDGE,"E64.MirrorCS")])]});
            var Q26;
            Q26=makeQuery(id+"F2.opExtrude","SWEPT_EDGE",EDGE,{"disambiguationData":[OSD([sQuery(id+"F0.wireOp",EDGE,"E52.MirrorCS"),sQuery(id+"F0.wireOp",EDGE,"E64.MirrorCS")])]});
            var Q27;
            Q27=makeQuery(id+"F2.opExtrude","SWEPT_EDGE",EDGE,{"disambiguationData":[OSD([sQuery(id+"F0.wireOp",EDGE,"E52.MirrorCS"),sQuery(id+"F0.wireOp",EDGE,"E82.MirrorCS")])]});
            var Q28;
            Q28=makeQuery(id+"F2.opExtrude","SWEPT_EDGE",EDGE,{"disambiguationData":[OSD([sQuery(id+"F0.wireOp",EDGE,"E82.MirrorCS"),sQuery(id+"F0.wireOp",EDGE,"E94.MirrorCS")])]});
            var Q29;
            Q29=makeQuery(id+"F2.opExtrude","SWEPT_EDGE",EDGE,{"disambiguationData":[OSD([sQuery(id+"F0.wireOp",EDGE,"E76.MirrorCS"),sQuery(id+"F0.wireOp",EDGE,"E94.MirrorCS")])]});
            var Q30;
            Q30=makeQuery(id+"F1.opExtrude","SWEPT_EDGE",EDGE,{"disambiguationData":[OSD([sQuery(id+"F0.wireOp",EDGE,"E0.left"),sQuery(id+"F0.wireOp",EDGE,"E35.MirrorCS")])]});
            var Q31;
            Q31=makeQuery(id+"F1.opExtrude","SWEPT_EDGE",EDGE,{"disambiguationData":[OSD([sQuery(id+"F0.wireOp",EDGE,"E0.left"),sQuery(id+"F0.wireOp",EDGE,"E4.0")])]});
            var Q32;
            Q32=makeQuery(id+"F1.opExtrude","SWEPT_EDGE",EDGE,{"disambiguationData":[OSD([sQuery(id+"F0.wireOp",EDGE,"E33.MirrorCS"),sQuery(id+"F0.wireOp",EDGE,"E34.MirrorCS")])]});
            var Q33;
            Q33=makeQuery(id+"F1.opExtrude","SWEPT_EDGE",EDGE,{"disambiguationData":[OSD([sQuery(id+"F0.wireOp",EDGE,"E4.0"),sQuery(id+"F0.wireOp",EDGE,"E34.MirrorCS")])]});
            var Q34;
            Q34=makeQuery(id+"F1.opExtrude","SWEPT_EDGE",EDGE,{"disambiguationData":[OSD([sQuery(id+"F0.wireOp",EDGE,"E32.MirrorCS"),sQuery(id+"F0.wireOp",EDGE,"E33.MirrorCS")])]});
            var Q35;
            Q35=makeQuery(id+"F1.opExtrude","SWEPT_EDGE",EDGE,{"disambiguationData":[OSD([sQuery(id+"F0.wireOp",EDGE,"E30.MirrorCS"),sQuery(id+"F0.wireOp",EDGE,"E31.MirrorCS")])]});
            var Q36;
            Q36=makeQuery(id+"F1.opExtrude","SWEPT_EDGE",EDGE,{"disambiguationData":[OSD([sQuery(id+"F0.wireOp",EDGE,"E29.MirrorCS"),sQuery(id+"F0.wireOp",EDGE,"E30.MirrorCS")])]});
            var Q37;
            Q37=makeQuery(id+"F1.opExtrude","SWEPT_EDGE",EDGE,{"disambiguationData":[OSD([sQuery(id+"F0.wireOp",EDGE,"E27.MirrorC"),sQuery(id+"F0.wireOp",EDGE,"E29.MirrorCS")])]});
            var Q38;
            Q38=makeQuery(id+"F1.opExtrude","SWEPT_EDGE",EDGE,{"disambiguationData":[OSD([sQuery(id+"F0.wireOp",EDGE,"E0.left"),sQuery(id+"F0.wireOp",EDGE,"E21")])]});
            var Q39;
            Q39=makeQuery(id+"F1.opExtrude","SWEPT_EDGE",EDGE,{"disambiguationData":[OSD([sQuery(id+"F0.wireOp",EDGE,"E0.left"),sQuery(id+"F0.wireOp",EDGE,"E4.1")])]});
            var Q40;
            Q40=makeQuery(id+"F1.opExtrude","SWEPT_EDGE",EDGE,{"disambiguationData":[OSD([sQuery(id+"F0.wireOp",EDGE,"E14.right"),sQuery(id+"F0.wireOp",EDGE,"E20.top")])]});
            var Q41;
            Q41=makeQuery(id+"F1.opExtrude","SWEPT_EDGE",EDGE,{"disambiguationData":[OSD([sQuery(id+"F0.wireOp",EDGE,"E14.right"),sQuery(id+"F0.wireOp",EDGE,"E15.top")])]});
            var Q42;
            Q42=makeQuery(id+"F1.opExtrude","SWEPT_EDGE",EDGE,{"disambiguationData":[OSD([sQuery(id+"F0.wireOp",EDGE,"E15.top"),sQuery(id+"F0.wireOp",EDGE,"E15.right")])]});
            var Q43;
            Q43=makeQuery(id+"F1.opExtrude","SWEPT_EDGE",EDGE,{"disambiguationData":[OSD([sQuery(id+"F0.wireOp",EDGE,"E12.bottom"),sQuery(id+"F0.wireOp",EDGE,"E16.right")])]});
            var Q44;
            Q44=makeQuery(id+"F1.opExtrude","SWEPT_EDGE",EDGE,{"disambiguationData":[OSD([sQuery(id+"F0.wireOp",EDGE,"E16.top"),sQuery(id+"F0.wireOp",EDGE,"E16.right")])]});
            var Q45;
            Q45=makeQuery(id+"F1.opExtrude","SWEPT_EDGE",EDGE,{"disambiguationData":[OSD([sQuery(id+"F0.wireOp",EDGE,"E12.bottom"),sQuery(id+"F0.wireOp",EDGE,"E18")])]});
            fillet(context, id + "F5", {"entities" : qUnion([Q0, Q1, Q2, Q3, Q4, Q5, Q6, Q7, Q8, Q9, Q10, Q11, Q12, Q13, Q14, Q15, Q16, Q17, Q18, Q19, Q20, Q21, Q22, Q23, Q24, Q25, Q26, Q27, Q28, Q29, Q30, Q31, Q32, Q33, Q34, Q35, Q36, Q37, Q38, Q39, Q40, Q41, Q42, Q43, Q44, Q45]), "radius" : .5 * mm, "tangentPropagation" : true, "allowEdgeOverflow" : false});
        }
        {
            var Q0;
            Q0=makeQuery(id+"F3.opExtrude","CAP_FACE",FACE,{"disambiguationData":[OSD([sQuery(id+"F0.wireOp",EDGE,"E110.MirrorC"),sQuery(id+"F0.wireOp",EDGE,"E116.MirrorCS"),sQuery(id+"F0.wireOp",EDGE,"E118.MirrorC"),sQuery(id+"F0.wireOp",EDGE,"E121.MirrorCS"),sQuery(id+"F0.wireOp",EDGE,"E122.MirrorCS"),sQuery(id+"F0.wireOp",EDGE,"E123.MirrorCS"),sQuery(id+"F0.wireOp",EDGE,"E124.MirrorCS"),sQuery(id+"F0.wireOp",EDGE,"E126.MirrorCS"),sQuery(id+"F0.wireOp",EDGE,"E127.MirrorCS"),sQuery(id+"F0.wireOp",EDGE,"E128.MirrorCS"),sQuery(id+"F0.wireOp",EDGE,"E129.MirrorCS"),sQuery(id+"F0.wireOp",EDGE,"E130.MirrorCS"),sQuery(id+"F0.wireOp",EDGE,"E131.MirrorCS"),sQuery(id+"F0.wireOp",EDGE,"E132.MirrorCS"),sQuery(id+"F0.wireOp",EDGE,"E133.MirrorCS"),sQuery(id+"F0.wireOp",EDGE,"E120.MirrorCS"),sQuery(id+"F0.wireOp",EDGE,"E138.MirrorCS"),sQuery(id+"F0.wireOp",EDGE,"E139.MirrorCS"),sQuery(id+"F0.wireOp",EDGE,"E140.MirrorCS"),sQuery(id+"F0.wireOp",EDGE,"E141.MirrorCS"),sQuery(id+"F0.wireOp",EDGE,"E144.MirrorCS"),sQuery(id+"F0.wireOp",EDGE,"E146.MirrorC"),sQuery(id+"F0.wireOp",EDGE,"E147.MirrorC"),sQuery(id+"F0.wireOp",EDGE,"E148.MirrorC"),sQuery(id+"F0.wireOp",EDGE,"E149.MirrorCS"),sQuery(id+"F0.wireOp",EDGE,"E150.MirrorCS"),sQuery(id+"F0.wireOp",EDGE,"E153.MirrorC"),sQuery(id+"F0.wireOp",EDGE,"E154.MirrorC"),sQuery(id+"F0.wireOp",EDGE,"E155.MirrorC"),sQuery(id+"F0.wireOp",EDGE,"E157.MirrorCS"),sQuery(id+"F0.wireOp",EDGE,"E159.MirrorC"),sQuery(id+"F0.wireOp",EDGE,"E160.MirrorCS"),sQuery(id+"F0.wireOp",EDGE,"E161.MirrorC"),sQuery(id+"F0.wireOp",EDGE,"E162.MirrorCS"),sQuery(id+"F0.wireOp",EDGE,"E170.MirrorCS"),sQuery(id+"F0.wireOp",EDGE,"E171.MirrorCS"),sQuery(id+"F0.wireOp",EDGE,"E173.MirrorCS")])],"isStart":true});
            var sketch = newSketch(context, id + "F6", { "sketchPlane" : qUnion([Q0])});
            skLineSegment(sketch, "E175.bottom", {"start": v(-65.5, 33.1) * mm, "end": v(-59.5, 33.1) * mm});
            skLineSegment(sketch, "E175.top", {"start": v(-65.5, -33.1) * mm, "end": v(-59.5, -33.1) * mm});
            skLineSegment(sketch, "E175.left", {"start": v(-65.5, 33.1) * mm, "end": v(-65.5, -33.1) * mm});
            skLineSegment(sketch, "E175.right", {"start": v(-59.5, 33.1) * mm, "end": v(-59.5, -33.1) * mm});
            skSolve(sketch);
        }
        {
            var Q0;
            Q0 = qSketchRegion(id + "F6", true);
            extrude(context, id + "F7", {"entities" : qUnion([Q0]), "operationType" : NewBodyOperationType.REMOVE, "endBound" : BoundingType.THROUGH_ALL, "oppositeDirection" : true, "depth" : 40 * mm, "offsetDistance" : 25 * mm});
        }
        {
            var Q0;
            Q0=makeQuery(id+"F1.opExtrude","CAP_FACE",FACE,{"disambiguationData":[OSD([sQuery(id+"F0.wireOp",EDGE,"E0.top"),sQuery(id+"F0.wireOp",EDGE,"E0.left"),sQuery(id+"F0.wireOp",EDGE,"E1.bottom"),sQuery(id+"F0.wireOp",EDGE,"E1.right"),sQuery(id+"F0.wireOp",EDGE,"E2.filletArc"),sQuery(id+"F0.wireOp",EDGE,"E3.filletArc"),sQuery(id+"F0.wireOp",EDGE,"E4.0"),sQuery(id+"F0.wireOp",EDGE,"E4.1"),sQuery(id+"F0.wireOp",EDGE,"E4.3"),sQuery(id+"F0.wireOp",EDGE,"E5"),sQuery(id+"F0.wireOp",EDGE,"E6.0"),sQuery(id+"F0.wireOp",EDGE,"E8.left"),sQuery(id+"F0.wireOp",EDGE,"E9"),sQuery(id+"F0.wireOp",EDGE,"E10.0"),sQuery(id+"F0.wireOp",EDGE,"E14.right"),sQuery(id+"F0.wireOp",EDGE,"E15.top"),sQuery(id+"F0.wireOp",EDGE,"E15.right"),sQuery(id+"F0.wireOp",EDGE,"E12.bottom"),sQuery(id+"F0.wireOp",EDGE,"E16.top"),sQuery(id+"F0.wireOp",EDGE,"E16.right"),sQuery(id+"F0.wireOp",EDGE,"E17"),sQuery(id+"F0.wireOp",EDGE,"E18"),sQuery(id+"F0.wireOp",EDGE,"E20.bottom"),sQuery(id+"F0.wireOp",EDGE,"E20.top"),sQuery(id+"F0.wireOp",EDGE,"E21"),sQuery(id+"F0.wireOp",EDGE,"E24.MirrorC"),sQuery(id+"F0.wireOp",EDGE,"E25.MirrorC"),sQuery(id+"F0.wireOp",EDGE,"E26.MirrorC"),sQuery(id+"F0.wireOp",EDGE,"E27.MirrorC"),sQuery(id+"F0.wireOp",EDGE,"E29.MirrorCS"),sQuery(id+"F0.wireOp",EDGE,"E30.MirrorCS"),sQuery(id+"F0.wireOp",EDGE,"E31.MirrorCS"),sQuery(id+"F0.wireOp",EDGE,"E32.MirrorCS"),sQuery(id+"F0.wireOp",EDGE,"E33.MirrorCS"),sQuery(id+"F0.wireOp",EDGE,"E34.MirrorCS"),sQuery(id+"F0.wireOp",EDGE,"E35.MirrorCS"),sQuery(id+"F0.wireOp",EDGE,"E37"),sQuery(id+"F0.wireOp",EDGE,"E39")])],"isStart":true});
            var sketch = newSketch(context, id + "F8", { "sketchPlane" : qUnion([Q0])});
            skLineSegment(sketch, "E176.bottom", {"start": v(14.5, 33.1) * mm, "end": v(20.5, 33.1) * mm});
            skLineSegment(sketch, "E176.top", {"start": v(14.5, -33.1) * mm, "end": v(20.5, -33.1) * mm});
            skLineSegment(sketch, "E176.left", {"start": v(14.5, 33.1) * mm, "end": v(14.5, -33.1) * mm});
            skLineSegment(sketch, "E176.right", {"start": v(20.5, 33.1) * mm, "end": v(20.5, -33.1) * mm});
            skSolve(sketch);
        }
        {
            var Q0;
            Q0 = qSketchRegion(id + "F8", true);
            extrude(context, id + "F9", {"entities" : qUnion([Q0]), "operationType" : NewBodyOperationType.REMOVE, "oppositeDirection" : true, "depth" : 36 * mm, "offsetDistance" : 25 * mm});
        }
    });
